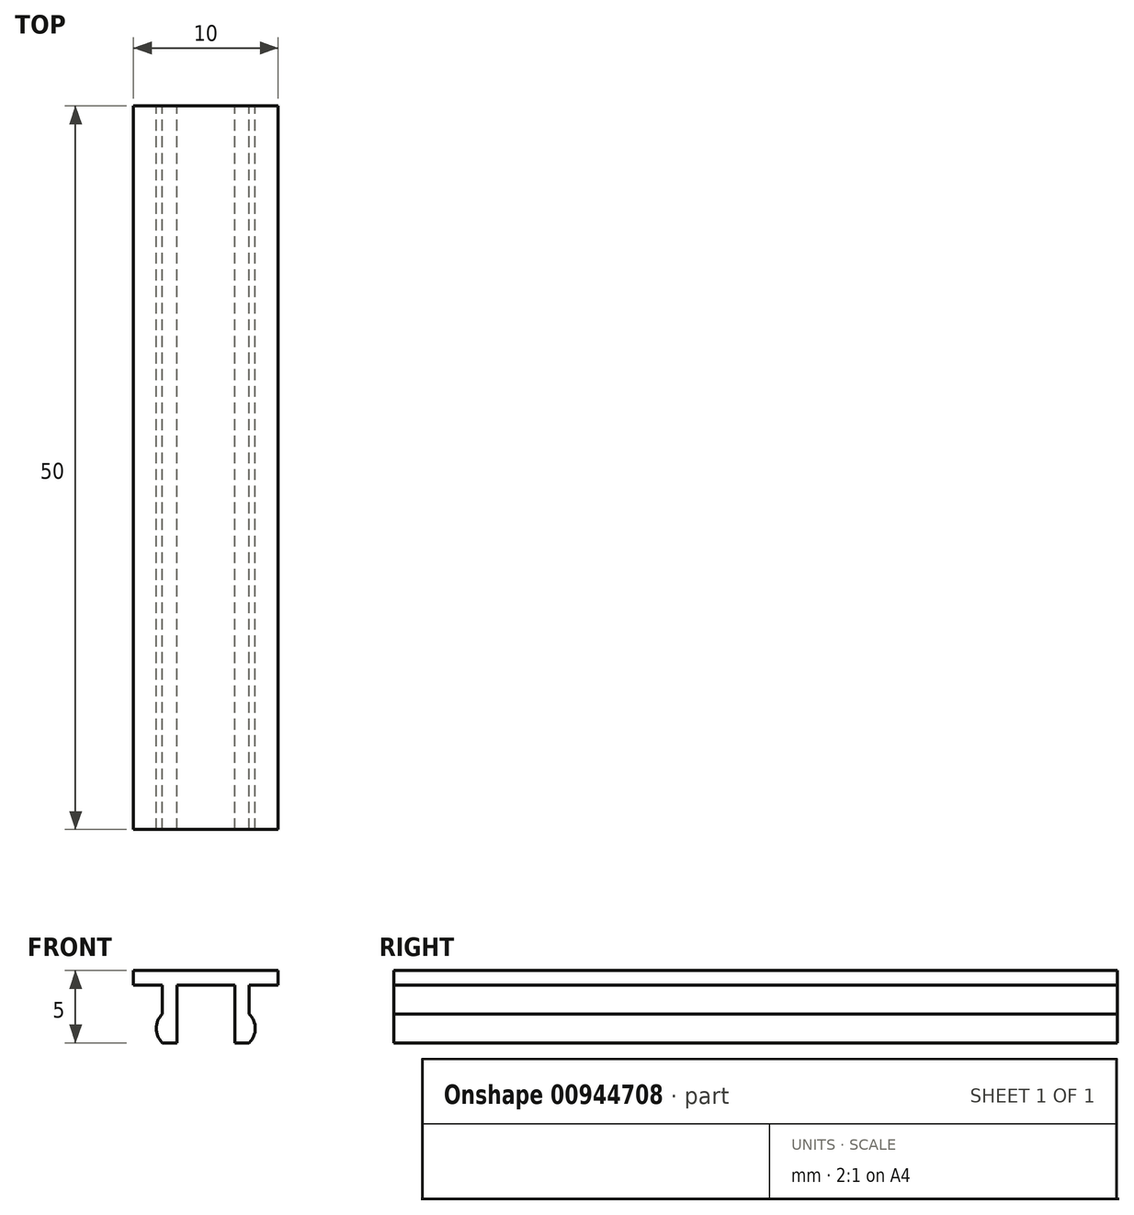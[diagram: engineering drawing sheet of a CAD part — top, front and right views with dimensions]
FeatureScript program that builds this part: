
annotation { "Feature Type Name" : "Feature", "Feature Type Description" : "" }
export const myFeature = defineFeature(function(context is Context, id is Id, definition is map)
    precondition{}
    {
        {
            var Q0;
            Q0=qCreatedBy(makeId("Front.planeOp"),FACE);
            var sketch = newSketch(context, id + "F0", { "sketchPlane" : qUnion([Q0])});
            skLineSegment(sketch, "E0", {"start": v(0, 1) * mm, "end": v(0, 0) * mm});
            skLineSegment(sketch, "E1", {"start": v(0, 1) * mm, "end": v(-5, 1) * mm});
            skLineSegment(sketch, "E2", {"start": v(-5, 1) * mm, "end": v(-5, 0) * mm});
            skLineSegment(sketch, "E3", {"start": v(-5, 0) * mm, "end": v(-3, 0) * mm});
            skLineSegment(sketch, "E4", {"start": v(-3, 0) * mm, "end": v(-3, -2) * mm});
            skLineSegment(sketch, "E5", {"start": v(-2, -4) * mm, "end": v(-2, 0) * mm});
            skLineSegment(sketch, "E6", {"start": v(-2, 0) * mm, "end": v(0, 0) * mm});
            skPoint(sketch, "E7.orphan", {"position": v(0, 30.88) * mm});
            skPoint(sketch, "E8.orphan", {"position": v(0, -25.74) * mm});
            skPoint(sketch, "E9.end.orphan", {"position": v(-3, -4) * mm});
            skArc(sketch, "E10", {"start": v(-3, -2) * mm, "mid": v(-3.41, -3) * mm, "end": v(-3, -4) * mm});
            skLineSegment(sketch, "E11", {"start": v(-2, -4) * mm, "end": v(-3, -4) * mm});
            skSolve(sketch);
        }
        {
            var Q0;
            Q0=makeQuery(id+"F0.imprint","IMPRINT",FACE,{"disambiguationData":[TD([[makeQuery(id+"F0.imprint","IMPRINT",EDGE,{"derivedFrom":sQuery(id+"F0.wireOp",EDGE,"E0")}),-1.0]])]});
            extrude(context, id + "F1", {"entities" : qUnion([Q0]), "depth" : 50 * mm, "offsetDistance" : 25 * mm});
        }
        {
            var Q0;
            Q0=makeQuery(id+"F1.opExtrude","SWEPT_BODY",BODY,{"disambiguationData":[OSD([sQuery(id+"F0.wireOp",EDGE,"E0"),sQuery(id+"F0.wireOp",EDGE,"E1"),sQuery(id+"F0.wireOp",EDGE,"E2"),sQuery(id+"F0.wireOp",EDGE,"E3"),sQuery(id+"F0.wireOp",EDGE,"E4"),sQuery(id+"F0.wireOp",EDGE,"E9"),sQuery(id+"F0.wireOp",EDGE,"3e6dd6af-6f10-4c2c-aadb-a9acdd0ee379"),sQuery(id+"F0.wireOp",EDGE,"E5"),sQuery(id+"F0.wireOp",EDGE,"E6")])]});
            var Q1;
            Q1=qCreatedBy(makeId("Right.planeOp"),FACE);
            mirror(context, id + "F2", {"operationType" : NewBodyOperationType.ADD, "entities" : qUnion([Q0]), "mirrorPlane" : qUnion([Q1])});
        }
    });
